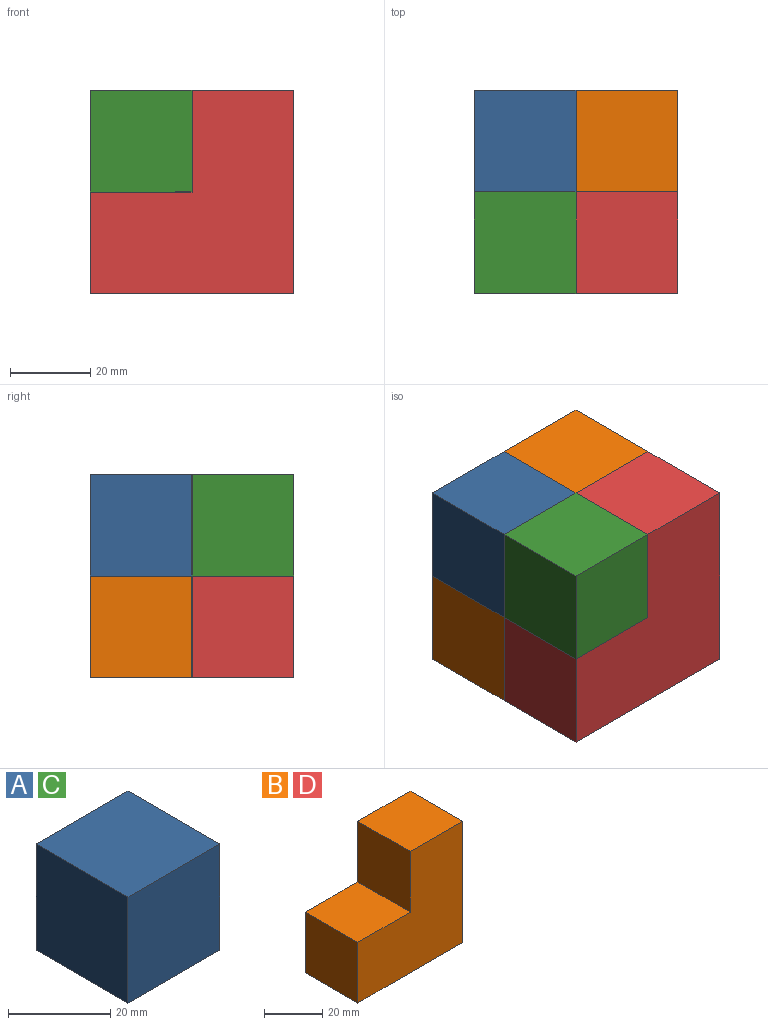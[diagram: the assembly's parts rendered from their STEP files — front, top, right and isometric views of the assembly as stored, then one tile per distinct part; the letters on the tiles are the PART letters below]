
ASSEMBLY  parts=4 mates=3
PART A: 6 faces, bbox 25.4x25.4x25.4 mm
  f0: plane 25.4x25.4mm, normal (-1,0,0), area 645.2mm2, adj f1,f3,f4,f5
  f1: plane 25.4x25.4mm, normal (0,0,-1), area 645.2mm2, adj f0,f2,f4,f5
  f2: plane 25.4x25.4mm, normal (1,0,0), area 645.2mm2, adj f1,f3,f4,f5
  f3: plane 25.4x25.4mm, normal (0,0,1), area 645.2mm2, adj f0,f2,f4,f5
  f4: plane 25.4x25.4mm, normal (0,-1,0), area 645.2mm2, adj f0,f1,f2,f3
  f5: plane 25.4x25.4mm, normal (0,1,0), area 645.2mm2, adj f0,f1,f2,f3
PART B: 8 faces, bbox 50.8x25.4x50.8 mm
  f0: plane 25.4x25.4mm, normal (0,0,1), area 645.2mm2, adj f1,f5,f6,f7
  f1: plane 25.4x25.4mm, normal (-1,0,0), area 645.2mm2, adj f0,f2,f6,f7
  f2: plane 50.8x25.4mm, normal (0,0,-1), area 1290.3mm2, adj f1,f3,f6,f7
  f3: plane 50.8x25.4mm, normal (1,0,0), area 1290.3mm2, adj f2,f4,f6,f7
  f4: plane 25.4x25.4mm, normal (0,0,1), area 645.2mm2, adj f3,f5,f6,f7
  f5: plane 25.4x25.4mm, normal (-1,0,0), area 645.2mm2, adj f0,f4,f6,f7
  f6: plane 50.8x50.8mm, normal (0,-1,0), area 1935.5mm2, adj f0,f1,f2,f3,f4,f5
  f7: plane 50.8x50.8mm, normal (0,1,0), area 1935.5mm2, adj f0,f1,f2,f3,f4,f5
PART C: same geometry as A
PART D: same geometry as B
PLACE A rot(axis=(-0.58,0.58,-0.58),120deg) t=(-33.45,18.87,16.23)mm
PLACE B t=(17.35,44.27,-9.17)mm
PLACE C rot(axis=(0,0,-1),90deg) t=(-8.05,-6.53,16.23)mm
PLACE D t=(17.35,18.87,-9.17)mm fixed
MATE fastened C.f3 <-> D.f4  axis (0,0,1) through (-8.05,-6.53,41.63)mm
MATE fastened D.f7 <-> B.f6  axis (0,1,0) through (-8.05,18.87,16.23)mm
MATE fastened A.f0 <-> B.f7  axis (0,1,0) through (-8.05,44.27,16.23)mm
